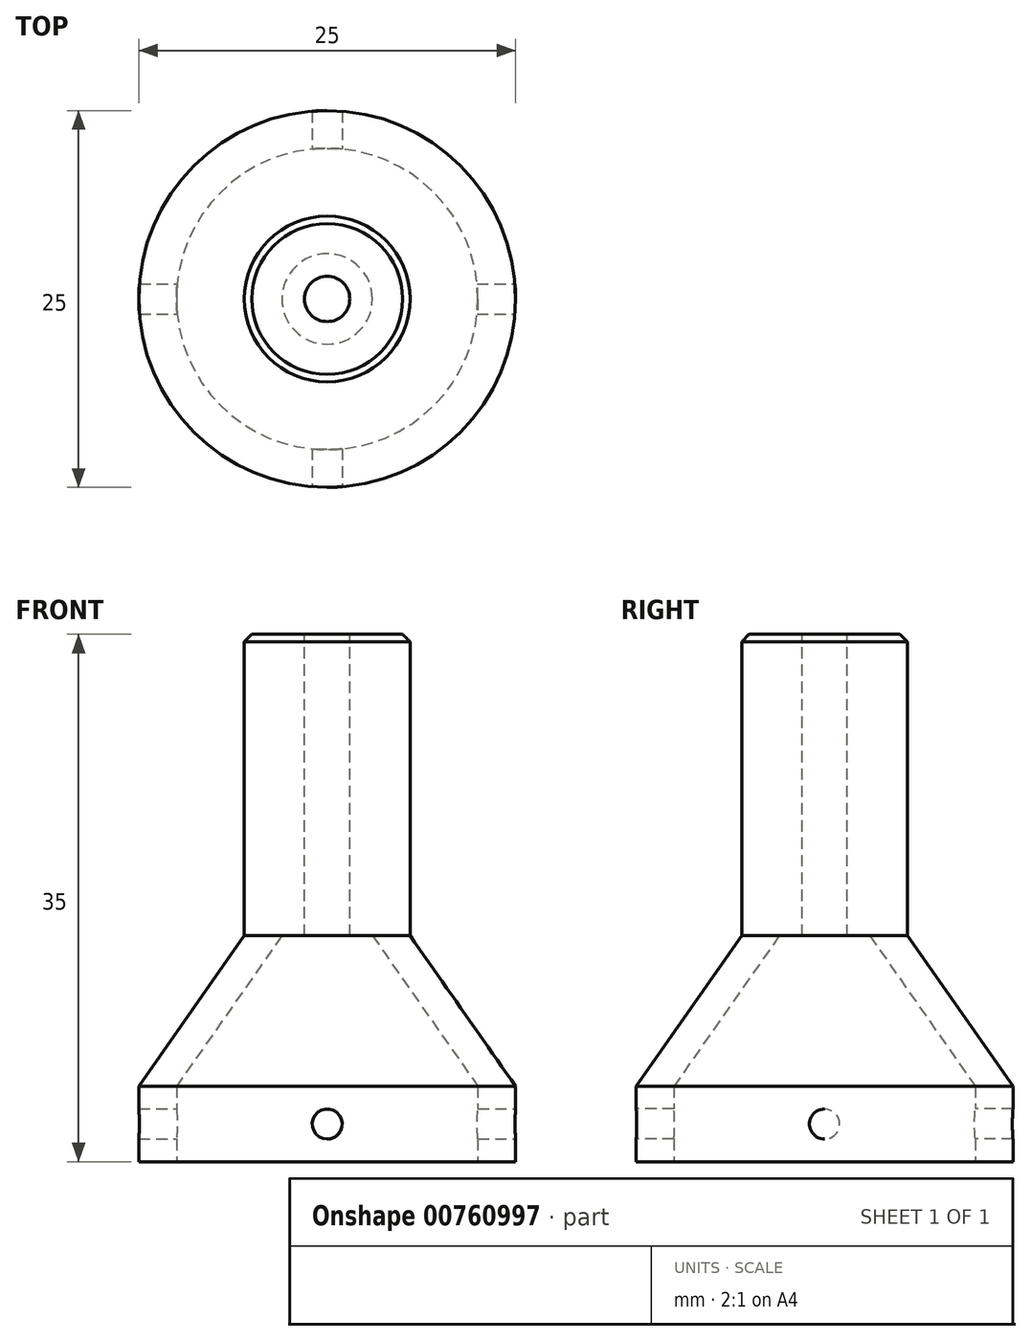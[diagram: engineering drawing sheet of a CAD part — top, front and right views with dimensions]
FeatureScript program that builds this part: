
annotation { "Feature Type Name" : "Feature", "Feature Type Description" : "" }
export const myFeature = defineFeature(function(context is Context, id is Id, definition is map)
    precondition{}
    {
        {
            var Q0;
            Q0=qCreatedBy(makeId("Top.planeOp"),FACE);
            var sketch = newSketch(context, id + "F0", { "sketchPlane" : qUnion([Q0])});
            skCircle(sketch, "E0", {"center": v(0, 0) * mm, "radius": 10 * mm});
            skCircle(sketch, "E1", {"center": v(0, 0) * mm, "radius": 12.5 * mm});
            skSolve(sketch);
        }
        {
            var Q0;
            Q0 = qSketchRegion(id + "F0", true);
            extrude(context, id + "F1", {"entities" : qUnion([Q0]), "depth" : 5 * mm, "offsetDistance" : 25 * mm});
        }
        {
            var Q0;
            Q0=qCreatedBy(makeId("Top.planeOp"),FACE);
            cPlane(context, id + "F2", {"entities" : qUnion([Q0]), "cplaneType" : CPlaneType.OFFSET, "offset" : 15 * mm, "width" : 150 * mm, "height" : 150 * mm});
        }
        {
            var Q0;
            Q0=qCreatedBy(id+"F2.planeOp",FACE);
            var sketch = newSketch(context, id + "F3", { "sketchPlane" : qUnion([Q0])});
            skCircle(sketch, "E2", {"center": v(0, 0) * mm, "radius": 5.5 * mm});
            skSolve(sketch);
        }
        {
            var Q0;
            Q0=makeQuery(id+"F1.opExtrude","CAP_FACE",FACE,{"disambiguationData":[OSD([sQuery(id+"F0.wireOp",EDGE,"E0"),sQuery(id+"F0.wireOp",EDGE,"E1")])],"isStart":false});
            var sketch = newSketch(context, id + "F4", { "sketchPlane" : qUnion([Q0])});
            skCircle(sketch, "E3.0", {"center": v(0, 0) * mm, "radius": 12.5 * mm});
            skSolve(sketch);
        }
        {
            var Q1;
            Q1 = qSketchRegion(id + "F4", true);
            var Q2;
            Q2 = qSketchRegion(id + "F3", true);
            loft(context, id + "F5", {"operationType" : NewBodyOperationType.ADD, "sheetProfilesArray" : [{ "sheetProfileEntities" : qUnion([Q1]) }, { "sheetProfileEntities" : qUnion([Q2]) }]});
        }
        {
            var Q0;
            Q0=makeQuery(id+"F4.imprint","IMPRINT",FACE,{"disambiguationData":[TD([[makeQuery(id+"F4.imprint","IMPRINT",EDGE,{"derivedFrom":sQuery(id+"F4.wireOp",EDGE,"E3.0")}),1.0]])]});
            var sketch = newSketch(context, id + "F6", { "sketchPlane" : qUnion([Q0])});
            skCircle(sketch, "E4", {"center": v(0, 0) * mm, "radius": 10 * mm});
            skSolve(sketch);
        }
        {
            var Q0;
            Q0=qCreatedBy(id+"F2.planeOp",FACE);
            var sketch = newSketch(context, id + "F7", { "sketchPlane" : qUnion([Q0])});
            skCircle(sketch, "E5", {"center": v(0, 0) * mm, "radius": 3 * mm});
            skSolve(sketch);
        }
        {
            var Q1;
            Q1 = qSketchRegion(id + "F6", true);
            var Q2;
            Q2 = qSketchRegion(id + "F7", true);
            loft(context, id + "F8", {"operationType" : NewBodyOperationType.REMOVE, "sheetProfilesArray" : [{ "sheetProfileEntities" : qUnion([Q1]) }, { "sheetProfileEntities" : qUnion([Q2]) }]});
        }
        {
            var Q0;
            Q0=makeQuery(id+"F5.opLoft","CAP_FACE",FACE,{"disambiguationData":[OSD([makeQuery(id+"F3.imprint","IMPRINT",FACE,{"disambiguationData":[TD([[makeQuery(id+"F3.imprint","IMPRINT",EDGE,{"derivedFrom":sQuery(id+"F3.wireOp",EDGE,"E2")}),1.0]])]})])],"isStart":true});
            var sketch = newSketch(context, id + "F9", { "sketchPlane" : qUnion([Q0])});
            skCircle(sketch, "E6", {"center": v(0, 0) * mm, "radius": 5.5 * mm});
            skSolve(sketch);
        }
        {
            var Q0;
            Q0 = qSketchRegion(id + "F9", true);
            extrude(context, id + "F10", {"entities" : qUnion([Q0]), "operationType" : NewBodyOperationType.ADD, "depth" : 20 * mm, "offsetDistance" : 25 * mm});
        }
        {
            var Q0;
            Q0=makeQuery(id+"F10.opExtrude","CAP_EDGE",EDGE,{"disambiguationData":[OSD([sQuery(id+"F9.wireOp",EDGE,"E6")])],"isStart":false});
            chamfer(context, id + "F11", {"entities" : qUnion([Q0]), "width" : 0.5 * mm, "tangentPropagation" : true});
        }
        {
            var Q0;
            Q0=qCreatedBy(makeId("Right.planeOp"),FACE);
            var sketch = newSketch(context, id + "F12", { "sketchPlane" : qUnion([Q0])});
            skCircle(sketch, "E7", {"center": v(0, 2.5) * mm, "radius": 1 * mm});
            skSolve(sketch);
        }
        {
            var Q0;
            Q0 = qSketchRegion(id + "F12", true);
            extrude(context, id + "F13", {"entities" : qUnion([Q0]), "operationType" : NewBodyOperationType.REMOVE, "endBound" : BoundingType.SYMMETRIC, "oppositeDirection" : true, "depth" : 50 * mm, "offsetDistance" : 25 * mm});
        }
        {
            var Q0;
            Q0=qCreatedBy(makeId("Front.planeOp"),FACE);
            var sketch = newSketch(context, id + "F14", { "sketchPlane" : qUnion([Q0])});
            skCircle(sketch, "E8", {"center": v(0, 2.5) * mm, "radius": 1 * mm});
            skSolve(sketch);
        }
        {
            var Q0;
            Q0 = qSketchRegion(id + "F14", true);
            extrude(context, id + "F15", {"entities" : qUnion([Q0]), "operationType" : NewBodyOperationType.REMOVE, "endBound" : BoundingType.SYMMETRIC, "oppositeDirection" : true, "depth" : 50 * mm, "offsetDistance" : 25 * mm});
        }
        {
            var Q0;
            Q0=makeQuery(id+"F10.opExtrude","CAP_FACE",FACE,{"disambiguationData":[OSD([sQuery(id+"F9.wireOp",EDGE,"E6")])],"isStart":false});
            var sketch = newSketch(context, id + "F16", { "sketchPlane" : qUnion([Q0])});
            skCircle(sketch, "E9", {"center": v(0, 0) * mm, "radius": 1.5 * mm});
            skSolve(sketch);
        }
        {
            var Q0;
            Q0 = qSketchRegion(id + "F16", true);
            extrude(context, id + "F17", {"entities" : qUnion([Q0]), "operationType" : NewBodyOperationType.REMOVE, "endBound" : BoundingType.THROUGH_ALL, "oppositeDirection" : true, "depth" : 25 * mm, "offsetDistance" : 25 * mm});
        }
    });
